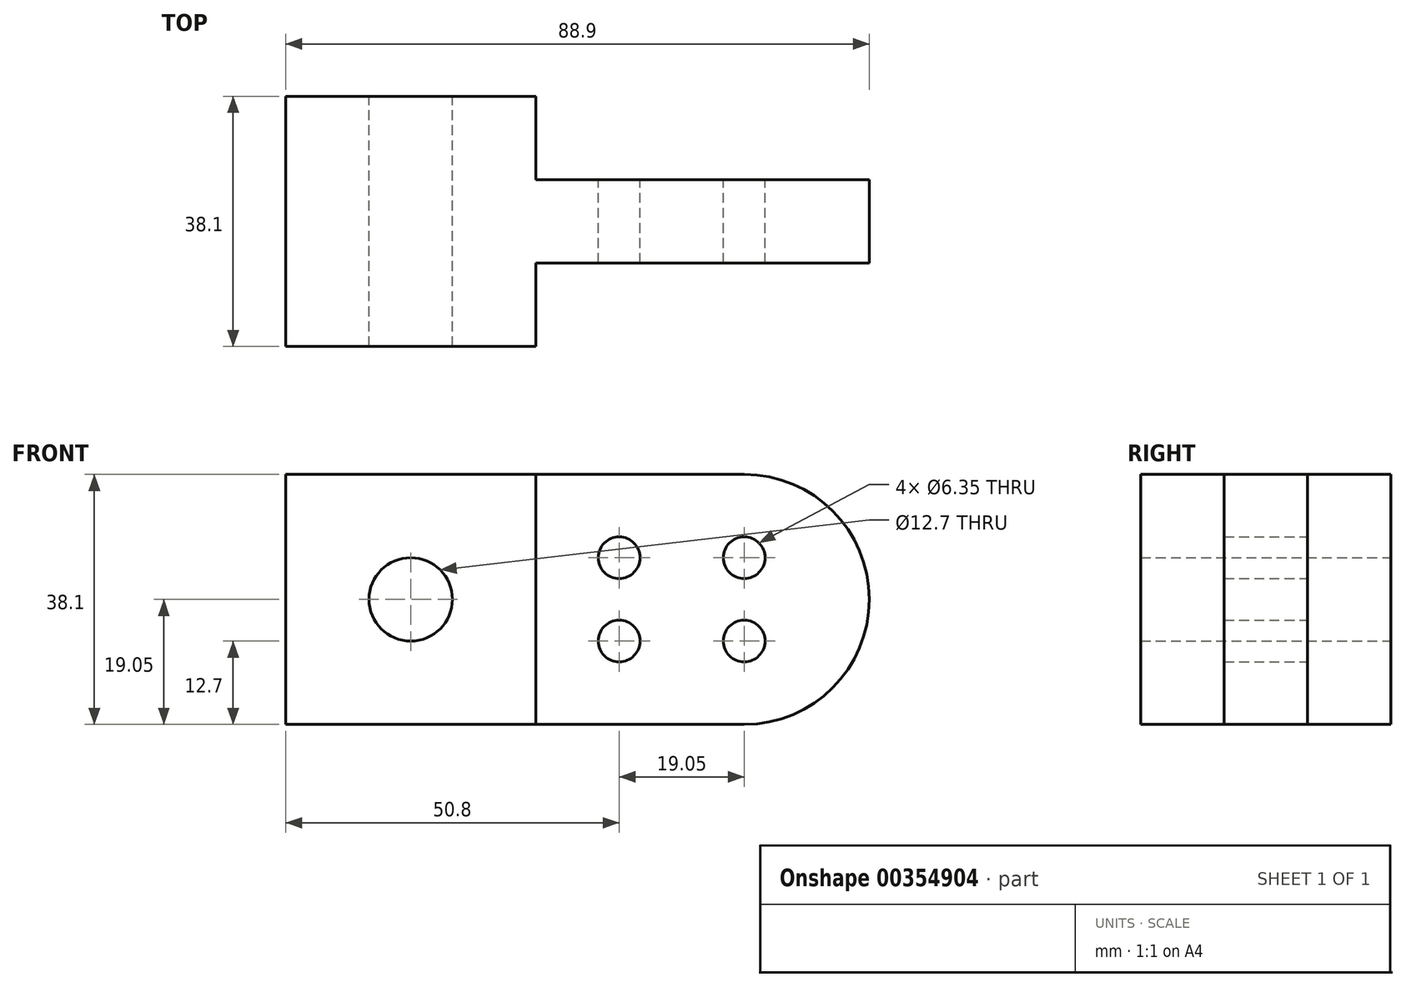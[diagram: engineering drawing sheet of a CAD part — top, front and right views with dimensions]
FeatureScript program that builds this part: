
annotation { "Feature Type Name" : "Feature", "Feature Type Description" : "" }
export const myFeature = defineFeature(function(context is Context, id is Id, definition is map)
    precondition{}
    {
        {
            var Q0;
            Q0=qCreatedBy(makeId("Front.planeOp"),FACE);
            var sketch = newSketch(context, id + "F0", { "sketchPlane" : qUnion([Q0])});
            skLineSegment(sketch, "E0.bottom", {"start": v(0, 0) * mm, "end": v(38.1, 0) * mm});
            skLineSegment(sketch, "E0.top", {"start": v(0, 38.1) * mm, "end": v(38.1, 38.1) * mm});
            skLineSegment(sketch, "E0.left", {"start": v(0, 0) * mm, "end": v(0, 38.1) * mm});
            skLineSegment(sketch, "E0.right", {"start": v(38.1, 0) * mm, "end": v(38.1, 38.1) * mm});
            skLineSegment(sketch, "E1", {"start": v(38.1, 38.1) * mm, "end": v(69.85, 38.1) * mm});
            skArc(sketch, "E2", {"start": v(69.85, 38.1) * mm, "mid": v(88.9, 19.05) * mm, "end": v(69.85, 0) * mm});
            skLineSegment(sketch, "E3", {"start": v(38.1, 0) * mm, "end": v(69.85, 0) * mm});
            skCircle(sketch, "E4", {"center": v(19.05, 19.05) * mm, "radius": 6.35 * mm});
            skPoint(sketch, "E4.centerSnap0", {"position": v(0, 19.05) * mm});
            skPoint(sketch, "E4.centerSnap1", {"position": v(19.05, 38.1) * mm});
            skLineSegment(sketch, "E5", {"start": v(69.85, 38.1) * mm, "end": v(69.85, 0) * mm, "construction": true});
            skLineSegment(sketch, "E6", {"start": v(88.9, 19.05) * mm, "end": v(38.1, 19.05) * mm, "construction": true});
            skCircle(sketch, "E7", {"center": v(50.8, 25.4) * mm, "radius": 3.18 * mm});
            skCircle(sketch, "E8", {"center": v(69.85, 25.4) * mm, "radius": 3.18 * mm});
            skCircle(sketch, "E9", {"center": v(50.8, 12.7) * mm, "radius": 3.18 * mm});
            skCircle(sketch, "E10", {"center": v(69.85, 12.7) * mm, "radius": 3.18 * mm});
            skSolve(sketch);
        }
        {
            var Q0;
            Q0=makeQuery(id+"F0.imprint","IMPRINT",FACE,{"disambiguationData":[TD([[makeQuery(id+"F0.imprint","IMPRINT",EDGE,{"derivedFrom":sQuery(id+"F0.wireOp",EDGE,"E0.right")}),-1.0]])]});
            extrude(context, id + "F1", {"entities" : qUnion([Q0]), "endBound" : BoundingType.SYMMETRIC, "depth" : 12.7 * mm});
        }
        {
            var Q0;
            Q0=makeQuery(id+"F0.imprint","IMPRINT",FACE,{"disambiguationData":[TD([[makeQuery(id+"F0.imprint","IMPRINT",EDGE,{"derivedFrom":sQuery(id+"F0.wireOp",EDGE,"E0.bottom")}),1.0]])]});
            extrude(context, id + "F2", {"entities" : qUnion([Q0]), "operationType" : NewBodyOperationType.ADD, "endBound" : BoundingType.SYMMETRIC, "depth" : 38.1 * mm});
        }
    });
